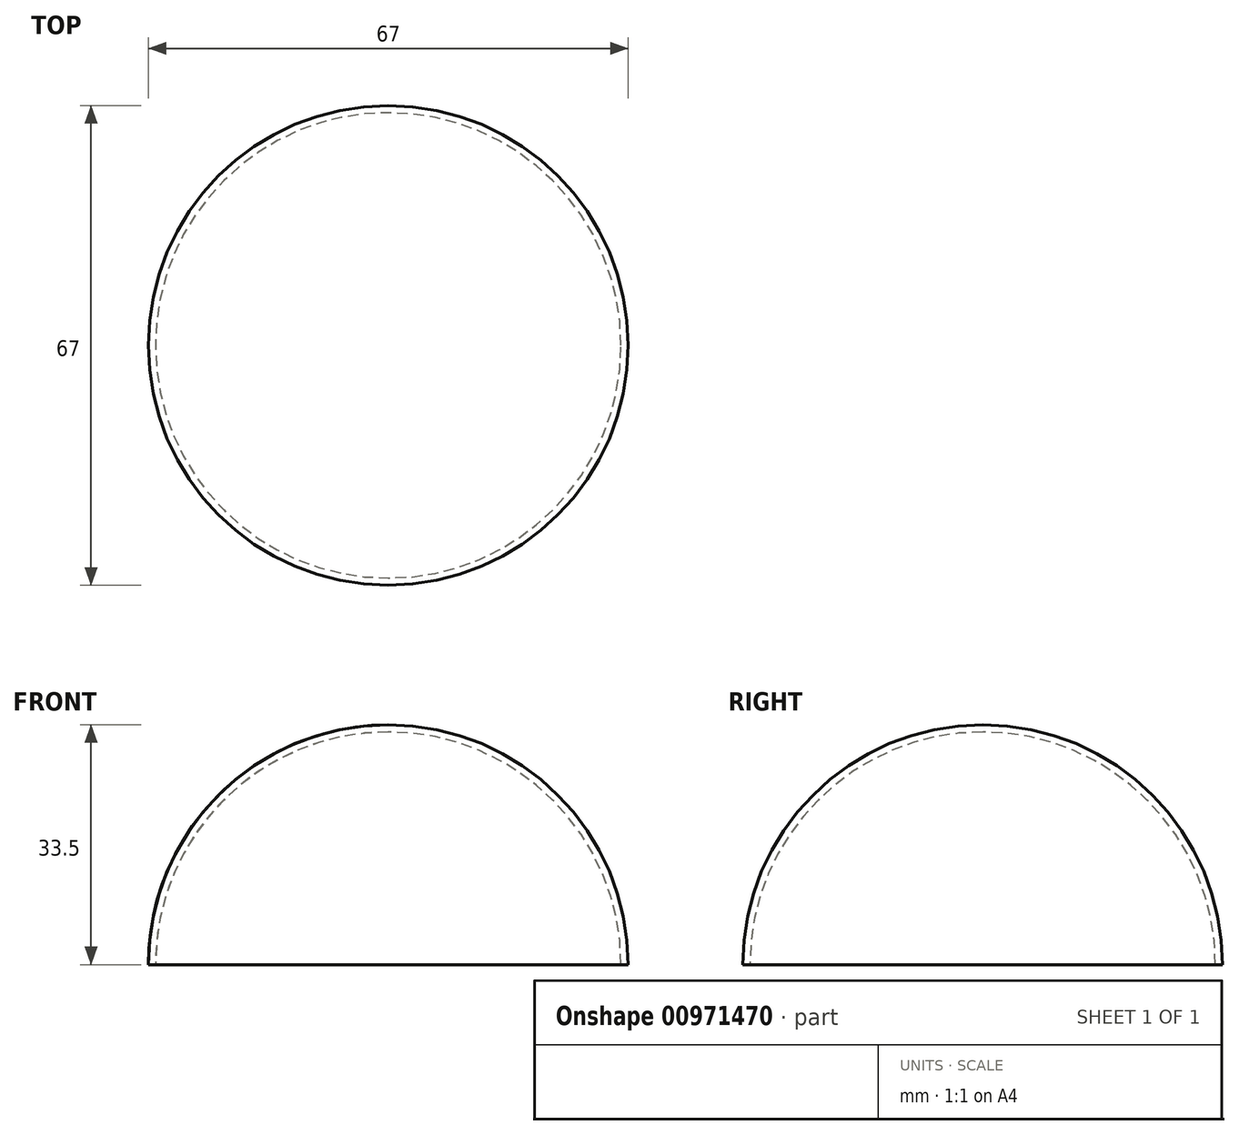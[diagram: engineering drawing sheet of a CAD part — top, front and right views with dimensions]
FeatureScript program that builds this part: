
annotation { "Feature Type Name" : "Feature", "Feature Type Description" : "" }
export const myFeature = defineFeature(function(context is Context, id is Id, definition is map)
    precondition{}
    {
        {
            var Q0;
            Q0=qCreatedBy(makeId("Front.planeOp"),FACE);
            var sketch = newSketch(context, id + "F0", { "sketchPlane" : qUnion([Q0])});
            skLineSegment(sketch, "E0", {"start": v(-33.5, 0) * mm, "end": v(-32.5, 0) * mm});
            skLineSegment(sketch, "E1", {"start": v(0, 32.5) * mm, "end": v(0, 33.5) * mm});
            skLineSegment(sketch, "E2", {"start": v(0, 33.5) * mm, "end": v(0, 33.5) * mm});
            skArc(sketch, "E3", {"start": v(0, 33.5) * mm, "mid": v(-23.69, 23.69) * mm, "end": v(-33.5, 0) * mm});
            skArc(sketch, "E4", {"start": v(-33.5, 0) * mm, "mid": v(23.69, -23.69) * mm, "end": v(0, 33.5) * mm, "construction": true});
            skArc(sketch, "E5", {"start": v(0, 32.5) * mm, "mid": v(-22.98, 22.98) * mm, "end": v(-32.5, 0) * mm});
            skArc(sketch, "E6", {"start": v(-32.5, 0) * mm, "mid": v(22.98, -22.98) * mm, "end": v(0, 32.5) * mm, "construction": true});
            skArc(sketch, "E7.0", {"start": v(0, 31.5) * mm, "mid": v(-22.27, 22.27) * mm, "end": v(-31.5, 0) * mm});
            skLineSegment(sketch, "E8", {"start": v(-32.5, 0) * mm, "end": v(-31.5, 0) * mm});
            skLineSegment(sketch, "E9", {"start": v(0, 31.5) * mm, "end": v(0, 32.5) * mm});
            skSolve(sketch);
        }
        {
            var Q0;
            Q0=makeQuery(id+"F0.imprint","IMPRINT",FACE,{"disambiguationData":[TD([[makeQuery(id+"F0.imprint","IMPRINT",EDGE,{"derivedFrom":sQuery(id+"F0.wireOp",EDGE,"E0")}),1.0]])]});
            var Q1;
            Q1=sQuery(id+"F0.wireOp",EDGE,"E1");
            revolve(context, id + "F1", {"surfaceOperationType" : NewSurfaceOperationType.NEW, "entities" : qUnion([Q0]), "axis" : qUnion([Q1]), "revolveType" : RevolveType.FULL});
        }
    });
